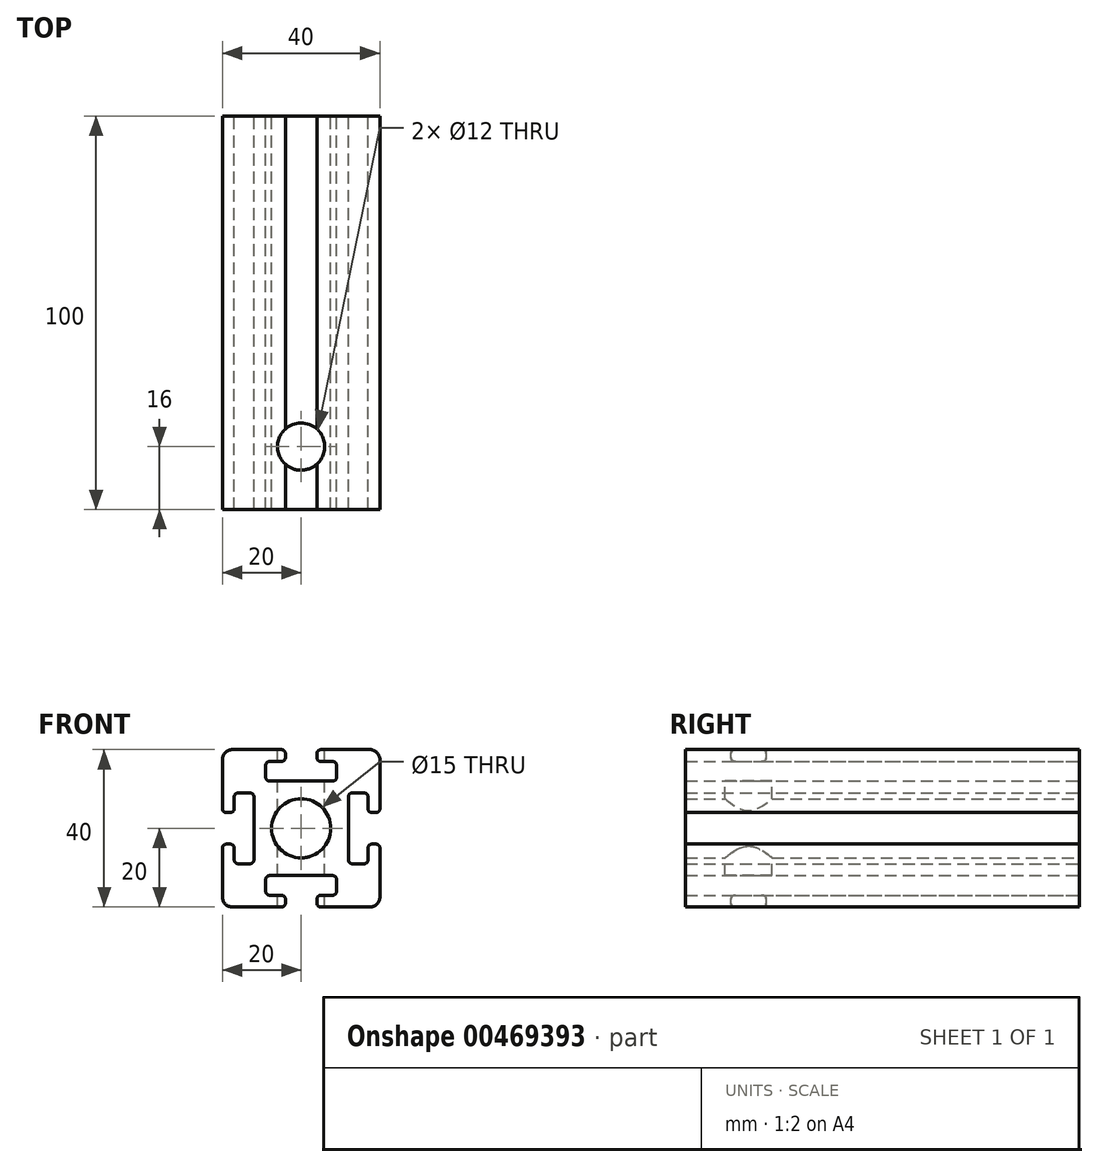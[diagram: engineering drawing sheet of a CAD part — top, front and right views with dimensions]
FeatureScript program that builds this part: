
annotation { "Feature Type Name" : "Feature", "Feature Type Description" : "" }
export const myFeature = defineFeature(function(context is Context, id is Id, definition is map)
    precondition{}
    {
        {
            var Q0;
            Q0=qCreatedBy(makeId("Front.planeOp"),FACE);
            var sketch = newSketch(context, id + "F0", { "sketchPlane" : qUnion([Q0])});
            skLineSegment(sketch, "E0.bottom", {"start": v(17.46, -20) * mm, "end": v(5, -20) * mm});
            skLineSegment(sketch, "E0.top", {"start": v(17.46, 20) * mm, "end": v(5, 20) * mm});
            skLineSegment(sketch, "E0.left", {"start": v(20, -17.46) * mm, "end": v(20, -5) * mm});
            skLineSegment(sketch, "E0.right", {"start": v(-20, -17.46) * mm, "end": v(-20, -5) * mm});
            skPoint(sketch, "E0.middle", {"position": v(0, 0) * mm});
            skPoint(sketch, "E1.visualSharp", {"position": v(20, 20) * mm});
            skArc(sketch, "E1.filletArc", {"start": v(20, 17.46) * mm, "mid": v(19.26, 19.26) * mm, "end": v(17.46, 20) * mm});
            skPoint(sketch, "E2.visualSharp", {"position": v(-20, 20) * mm});
            skArc(sketch, "E2.filletArc", {"start": v(-17.46, 20) * mm, "mid": v(-19.26, 19.26) * mm, "end": v(-20, 17.46) * mm});
            skPoint(sketch, "E3.visualSharp", {"position": v(-20, -20) * mm});
            skArc(sketch, "E3.filletArc", {"start": v(-20, -17.46) * mm, "mid": v(-19.26, -19.26) * mm, "end": v(-17.46, -20) * mm});
            skPoint(sketch, "E4.visualSharp", {"position": v(20, -20) * mm});
            skArc(sketch, "E4.filletArc", {"start": v(17.46, -20) * mm, "mid": v(19.26, -19.26) * mm, "end": v(20, -17.46) * mm});
            skLineSegment(sketch, "E5", {"start": v(-4, 19) * mm, "end": v(-4, 18) * mm});
            skLineSegment(sketch, "E6", {"start": v(-5, 17) * mm, "end": v(-8, 17) * mm});
            skLineSegment(sketch, "E7", {"start": v(-9, 16) * mm, "end": v(-9, 13) * mm});
            skLineSegment(sketch, "E8", {"start": v(-8, 12) * mm, "end": v(0, 12) * mm});
            skLineSegment(sketch, "E9", {"start": v(0, 0) * mm, "end": v(0, 25.62) * mm, "construction": true});
            skLineSegment(sketch, "E10.trimOffspring", {"start": v(-5, 20) * mm, "end": v(-17.46, 20) * mm});
            skPoint(sketch, "E11.visualSharp", {"position": v(-4, 20) * mm});
            skArc(sketch, "E11.filletArc", {"start": v(-4, 19) * mm, "mid": v(-4.3, 19.7) * mm, "end": v(-5, 20) * mm});
            skPoint(sketch, "E12.visualSharp", {"position": v(-9, 12) * mm});
            skArc(sketch, "E12.filletArc", {"start": v(-9, 13) * mm, "mid": v(-8.7, 12.3) * mm, "end": v(-8, 12) * mm});
            skPoint(sketch, "E13.visualSharp", {"position": v(-9, 17) * mm});
            skArc(sketch, "E13.filletArc", {"start": v(-8, 17) * mm, "mid": v(-8.7, 16.7) * mm, "end": v(-9, 16) * mm});
            skPoint(sketch, "E14.visualSharp", {"position": v(-4, 17) * mm});
            skArc(sketch, "E14.filletArc", {"start": v(-5, 17) * mm, "mid": v(-4.3, 17.3) * mm, "end": v(-4, 18) * mm});
            skLineSegment(sketch, "E15.MirrorCS", {"start": v(8, 12) * mm, "end": v(0, 12) * mm});
            skArc(sketch, "E16.MirrorCS", {"start": v(9, 13) * mm, "mid": v(8.7, 12.3) * mm, "end": v(8, 12) * mm});
            skLineSegment(sketch, "E17.MirrorCS", {"start": v(9, 16) * mm, "end": v(9, 13) * mm});
            skArc(sketch, "E18.MirrorCS", {"start": v(8, 17) * mm, "mid": v(8.7, 16.7) * mm, "end": v(9, 16) * mm});
            skLineSegment(sketch, "E19.MirrorCS", {"start": v(5, 17) * mm, "end": v(8, 17) * mm});
            skPoint(sketch, "E20.MirrorP", {"position": v(4, 17) * mm});
            skArc(sketch, "E21.MirrorCS", {"start": v(5, 17) * mm, "mid": v(4.3, 17.3) * mm, "end": v(4, 18) * mm});
            skLineSegment(sketch, "E22.MirrorCS", {"start": v(4, 19) * mm, "end": v(4, 18) * mm});
            skArc(sketch, "E23.MirrorCS", {"start": v(4, 19) * mm, "mid": v(4.3, 19.7) * mm, "end": v(5, 20) * mm});
            skLineSegment(sketch, "E24", {"start": v(0, 0) * mm, "end": v(20, 0) * mm, "construction": true});
            skPoint(sketch, "E25.1.0", {"position": v(20, 4) * mm});
            skPoint(sketch, "E25.1.1", {"position": v(12, 9) * mm});
            skLineSegment(sketch, "E25.1.2", {"start": v(16, 9) * mm, "end": v(13, 9) * mm});
            skLineSegment(sketch, "E25.1.3", {"start": v(17, 5) * mm, "end": v(17, 8) * mm});
            skLineSegment(sketch, "E25.1.4", {"start": v(17, -5) * mm, "end": v(17, -8) * mm});
            skPoint(sketch, "E25.1.5", {"position": v(17, 9) * mm});
            skPoint(sketch, "E25.1.6", {"position": v(17, 4) * mm});
            skLineSegment(sketch, "E25.1.7", {"start": v(12, 8) * mm, "end": v(12, 0) * mm});
            skLineSegment(sketch, "E25.1.8", {"start": v(16, -9) * mm, "end": v(13, -9) * mm});
            skLineSegment(sketch, "E25.1.9", {"start": v(12, -8) * mm, "end": v(12, 0) * mm});
            skPoint(sketch, "E25.1.10", {"position": v(17, -4) * mm});
            skArc(sketch, "E25.1.11", {"start": v(13, 9) * mm, "mid": v(12.3, 8.7) * mm, "end": v(12, 8) * mm});
            skArc(sketch, "E25.1.12", {"start": v(19, 4) * mm, "mid": v(19.7, 4.3) * mm, "end": v(20, 5) * mm});
            skArc(sketch, "E25.1.13", {"start": v(17, -5) * mm, "mid": v(17.3, -4.3) * mm, "end": v(18, -4) * mm});
            skArc(sketch, "E25.1.14", {"start": v(19, -4) * mm, "mid": v(19.7, -4.3) * mm, "end": v(20, -5) * mm});
            skArc(sketch, "E25.1.15", {"start": v(13, -9) * mm, "mid": v(12.3, -8.7) * mm, "end": v(12, -8) * mm});
            skArc(sketch, "E25.1.16", {"start": v(17, -8) * mm, "mid": v(16.7, -8.7) * mm, "end": v(16, -9) * mm});
            skArc(sketch, "E25.1.17", {"start": v(17, 5) * mm, "mid": v(17.3, 4.3) * mm, "end": v(18, 4) * mm});
            skArc(sketch, "E25.1.18", {"start": v(17, 8) * mm, "mid": v(16.7, 8.7) * mm, "end": v(16, 9) * mm});
            skLineSegment(sketch, "E25.1.19", {"start": v(19, -4) * mm, "end": v(18, -4) * mm});
            skLineSegment(sketch, "E25.1.20", {"start": v(19, 4) * mm, "end": v(18, 4) * mm});
            skPoint(sketch, "E25.2.0", {"position": v(4, -20) * mm});
            skPoint(sketch, "E25.2.1", {"position": v(9, -12) * mm});
            skLineSegment(sketch, "E25.2.2", {"start": v(9, -16) * mm, "end": v(9, -13) * mm});
            skLineSegment(sketch, "E25.2.3", {"start": v(5, -17) * mm, "end": v(8, -17) * mm});
            skLineSegment(sketch, "E25.2.4", {"start": v(-5, -17) * mm, "end": v(-8, -17) * mm});
            skPoint(sketch, "E25.2.5", {"position": v(9, -17) * mm});
            skPoint(sketch, "E25.2.6", {"position": v(4, -17) * mm});
            skLineSegment(sketch, "E25.2.7", {"start": v(8, -12) * mm, "end": v(0, -12) * mm});
            skLineSegment(sketch, "E25.2.8", {"start": v(-9, -16) * mm, "end": v(-9, -13) * mm});
            skLineSegment(sketch, "E25.2.9", {"start": v(-8, -12) * mm, "end": v(0, -12) * mm});
            skPoint(sketch, "E25.2.10", {"position": v(-4, -17) * mm});
            skArc(sketch, "E25.2.11", {"start": v(9, -13) * mm, "mid": v(8.7, -12.3) * mm, "end": v(8, -12) * mm});
            skArc(sketch, "E25.2.12", {"start": v(4, -19) * mm, "mid": v(4.3, -19.7) * mm, "end": v(5, -20) * mm});
            skArc(sketch, "E25.2.13", {"start": v(-5, -17) * mm, "mid": v(-4.3, -17.3) * mm, "end": v(-4, -18) * mm});
            skArc(sketch, "E25.2.14", {"start": v(-4, -19) * mm, "mid": v(-4.3, -19.7) * mm, "end": v(-5, -20) * mm});
            skArc(sketch, "E25.2.15", {"start": v(-9, -13) * mm, "mid": v(-8.7, -12.3) * mm, "end": v(-8, -12) * mm});
            skArc(sketch, "E25.2.16", {"start": v(-8, -17) * mm, "mid": v(-8.7, -16.7) * mm, "end": v(-9, -16) * mm});
            skArc(sketch, "E25.2.17", {"start": v(5, -17) * mm, "mid": v(4.3, -17.3) * mm, "end": v(4, -18) * mm});
            skArc(sketch, "E25.2.18", {"start": v(8, -17) * mm, "mid": v(8.7, -16.7) * mm, "end": v(9, -16) * mm});
            skLineSegment(sketch, "E25.2.19", {"start": v(-4, -19) * mm, "end": v(-4, -18) * mm});
            skLineSegment(sketch, "E25.2.20", {"start": v(4, -19) * mm, "end": v(4, -18) * mm});
            skPoint(sketch, "E25.3.0", {"position": v(-20, -4) * mm});
            skPoint(sketch, "E25.3.1", {"position": v(-12, -9) * mm});
            skLineSegment(sketch, "E25.3.2", {"start": v(-16, -9) * mm, "end": v(-13, -9) * mm});
            skLineSegment(sketch, "E25.3.3", {"start": v(-17, -5) * mm, "end": v(-17, -8) * mm});
            skLineSegment(sketch, "E25.3.4", {"start": v(-17, 5) * mm, "end": v(-17, 8) * mm});
            skPoint(sketch, "E25.3.5", {"position": v(-17, -9) * mm});
            skPoint(sketch, "E25.3.6", {"position": v(-17, -4) * mm});
            skLineSegment(sketch, "E25.3.7", {"start": v(-12, -8) * mm, "end": v(-12, 0) * mm});
            skLineSegment(sketch, "E25.3.8", {"start": v(-16, 9) * mm, "end": v(-13, 9) * mm});
            skLineSegment(sketch, "E25.3.9", {"start": v(-12, 8) * mm, "end": v(-12, 0) * mm});
            skPoint(sketch, "E25.3.10", {"position": v(-17, 4) * mm});
            skArc(sketch, "E25.3.11", {"start": v(-13, -9) * mm, "mid": v(-12.3, -8.7) * mm, "end": v(-12, -8) * mm});
            skArc(sketch, "E25.3.12", {"start": v(-19, -4) * mm, "mid": v(-19.7, -4.3) * mm, "end": v(-20, -5) * mm});
            skArc(sketch, "E25.3.13", {"start": v(-17, 5) * mm, "mid": v(-17.3, 4.3) * mm, "end": v(-18, 4) * mm});
            skArc(sketch, "E25.3.14", {"start": v(-19, 4) * mm, "mid": v(-19.7, 4.3) * mm, "end": v(-20, 5) * mm});
            skArc(sketch, "E25.3.15", {"start": v(-13, 9) * mm, "mid": v(-12.3, 8.7) * mm, "end": v(-12, 8) * mm});
            skArc(sketch, "E25.3.16", {"start": v(-17, 8) * mm, "mid": v(-16.7, 8.7) * mm, "end": v(-16, 9) * mm});
            skArc(sketch, "E25.3.17", {"start": v(-17, -5) * mm, "mid": v(-17.3, -4.3) * mm, "end": v(-18, -4) * mm});
            skArc(sketch, "E25.3.18", {"start": v(-17, -8) * mm, "mid": v(-16.7, -8.7) * mm, "end": v(-16, -9) * mm});
            skLineSegment(sketch, "E25.3.19", {"start": v(-19, 4) * mm, "end": v(-18, 4) * mm});
            skLineSegment(sketch, "E25.3.20", {"start": v(-19, -4) * mm, "end": v(-18, -4) * mm});
            skLineSegment(sketch, "E25.anchor1", {"start": v(0, 0) * mm, "end": v(-9, 12) * mm, "construction": true});
            skLineSegment(sketch, "E25.anchor2", {"start": v(0, 0) * mm, "end": v(-12, -9) * mm, "construction": true});
            skLineSegment(sketch, "E26.trimOffspring", {"start": v(20, 5) * mm, "end": v(20, 17.46) * mm});
            skLineSegment(sketch, "E27.trimOffspring", {"start": v(-5, -20) * mm, "end": v(-17.46, -20) * mm});
            skLineSegment(sketch, "E28.trimOffspring", {"start": v(-20, 5) * mm, "end": v(-20, 17.46) * mm});
            skCircle(sketch, "E29", {"center": v(0, 0) * mm, "radius": 7.5 * mm});
            skSolve(sketch);
        }
        {
            var Q0;
            Q0 = qSketchRegion(id + "F0", true);
            extrude(context, id + "F1", {"entities" : qUnion([Q0]), "depth" : 100 * mm});
        }
        {
            var Q0;
            Q0=makeQuery(id+"F1.opExtrude","SWEPT_FACE",FACE,{"disambiguationData":[OSD([sQuery(id+"F0.wireOp",EDGE,"E0.top")])]});
            var sketch = newSketch(context, id + "F2", { "sketchPlane" : qUnion([Q0])});
            skCircle(sketch, "E30", {"center": v(0, -84) * mm, "radius": 6 * mm});
            skSolve(sketch);
        }
        {
            var Q0;
            Q0 = qSketchRegion(id + "F2", true);
            extrude(context, id + "F3", {"entities" : qUnion([Q0]), "operationType" : NewBodyOperationType.REMOVE, "oppositeDirection" : true, "depth" : 254 * mm});
        }
    });
